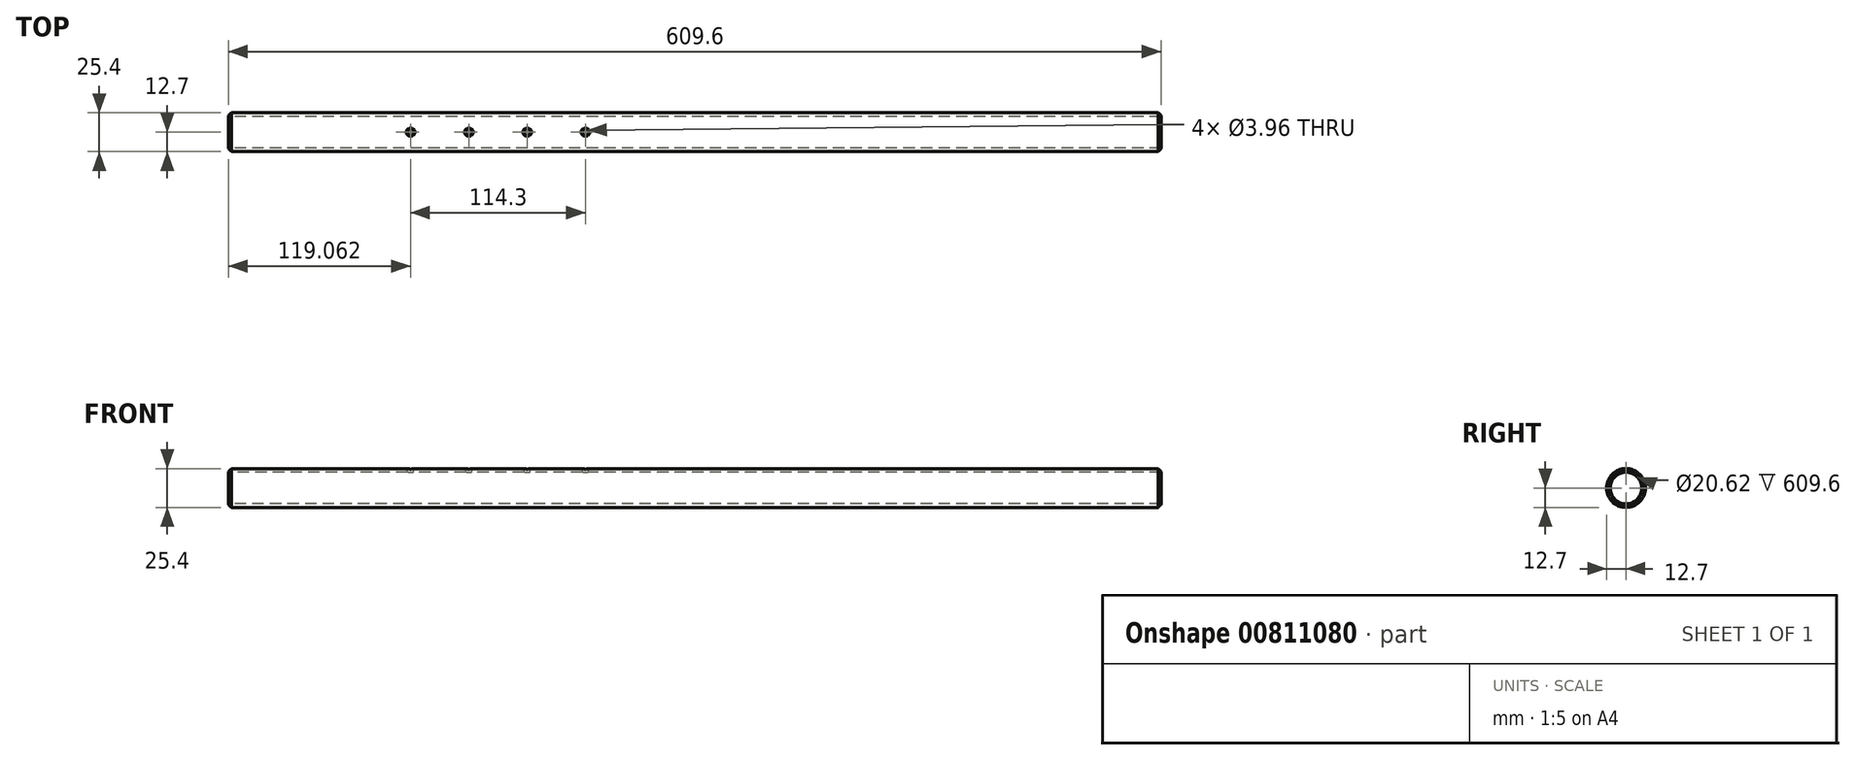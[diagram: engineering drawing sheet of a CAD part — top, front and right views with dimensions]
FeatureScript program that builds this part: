
annotation { "Feature Type Name" : "Feature", "Feature Type Description" : "" }
export const myFeature = defineFeature(function(context is Context, id is Id, definition is map)
    precondition{}
    {
        {
            var Q0;
            Q0=qCreatedBy(makeId("Right.planeOp"),FACE);
            var sketch = newSketch(context, id + "F0", { "sketchPlane" : qUnion([Q0])});
            skCircle(sketch, "E0", {"center": v(0, 0) * mm, "radius": 12.7 * mm});
            skCircle(sketch, "E1", {"center": v(0, 0) * mm, "radius": 10.31 * mm});
            skSolve(sketch);
        }
        {
            var Q0;
            Q0 = qSketchRegion(id + "F0", true);
            extrude(context, id + "F1", {"entities" : qUnion([Q0]), "depth" : 609.6 * mm, "offsetDistance" : 25.4 * mm, "symmetric" : true});
        }
        {
            var Q0;
            Q0=qCreatedBy(makeId("Top.planeOp"),FACE);
            cPlane(context, id + "F2", {"entities" : qUnion([Q0]), "cplaneType" : CPlaneType.OFFSET, "offset" : 12.7 * mm, "width" : 152.4 * mm, "height" : 152.4 * mm});
        }
        {
            var Q0;
            Q0=qCreatedBy(id+"F2.planeOp",FACE);
            var sketch = newSketch(context, id + "F3", { "sketchPlane" : qUnion([Q0])});
            skPoint(sketch, "E2", {"position": v(-185.74, 0) * mm});
            skPoint(sketch, "E3.1.0.0", {"position": v(-147.64, 0) * mm});
            skPoint(sketch, "E3.2.0.0", {"position": v(-109.54, 0) * mm});
            skPoint(sketch, "E3.3.0.0", {"position": v(-71.44, 0) * mm});
            skLineSegment(sketch, "E3.direction1", {"start": v(-185.74, 0) * mm, "end": v(-147.64, 0) * mm, "construction": true});
            skSolve(sketch);
        }
        {
            var Q0;
            Q0=sQuery(id+"F3.wireOp",VERTEX,"E2");
            var Q1;
            Q1=sQuery(id+"F3.wireOp",VERTEX,"E3.1.0.0");
            var Q2;
            Q2=sQuery(id+"F3.wireOp",VERTEX,"E3.2.0.0");
            var Q3;
            Q3=sQuery(id+"F3.wireOp",VERTEX,"E3.3.0.0");
            var Q4;
            Q4=makeQuery(id+"F1.opExtrude","SWEPT_BODY",BODY,{"disambiguationData":[OSD([sQuery(id+"F0.wireOp",EDGE,"E0"),sQuery(id+"F0.wireOp",EDGE,"E1")])]});
            hole(context, id + "F4", {"style" : HoleStyle.C_SINK, "endStyle" : HoleEndStyle.BLIND, "holeDiameter" : 3.96 * mm, "cSinkDiameter" : 5.7 * mm, "cSinkAngle" : 90 * degree, "majorDiameter" : 6.35 * mm, "holeDepth" : 12.7 * mm, "isTappedThrough" : true, "tappedDepth" : 12.7 * mm, "tapClearance" : 3, "startFromSketch" : true, "locations" : qUnion([Q0, Q1, Q2, Q3]), "scope" : qUnion([Q4])});
        }
        {
            var Q0;
            Q0=makeQuery(id+"F1.opExtrude","CAP_EDGE",EDGE,{"disambiguationData":[OSD([sQuery(id+"F0.wireOp",EDGE,"E0")])],"isStart":true});
            chamfer(context, id + "F5", {"entities" : qUnion([Q0]), "width" : 1.9 * mm, "tangentPropagation" : true});
        }
        {
            var Q0;
            Q0=makeQuery(id+"F1.opExtrude","CAP_EDGE",EDGE,{"disambiguationData":[OSD([sQuery(id+"F0.wireOp",EDGE,"E0")])],"isStart":false});
            chamfer(context, id + "F6", {"entities" : qUnion([Q0]), "width" : 1.9 * mm, "tangentPropagation" : true});
        }
    });
